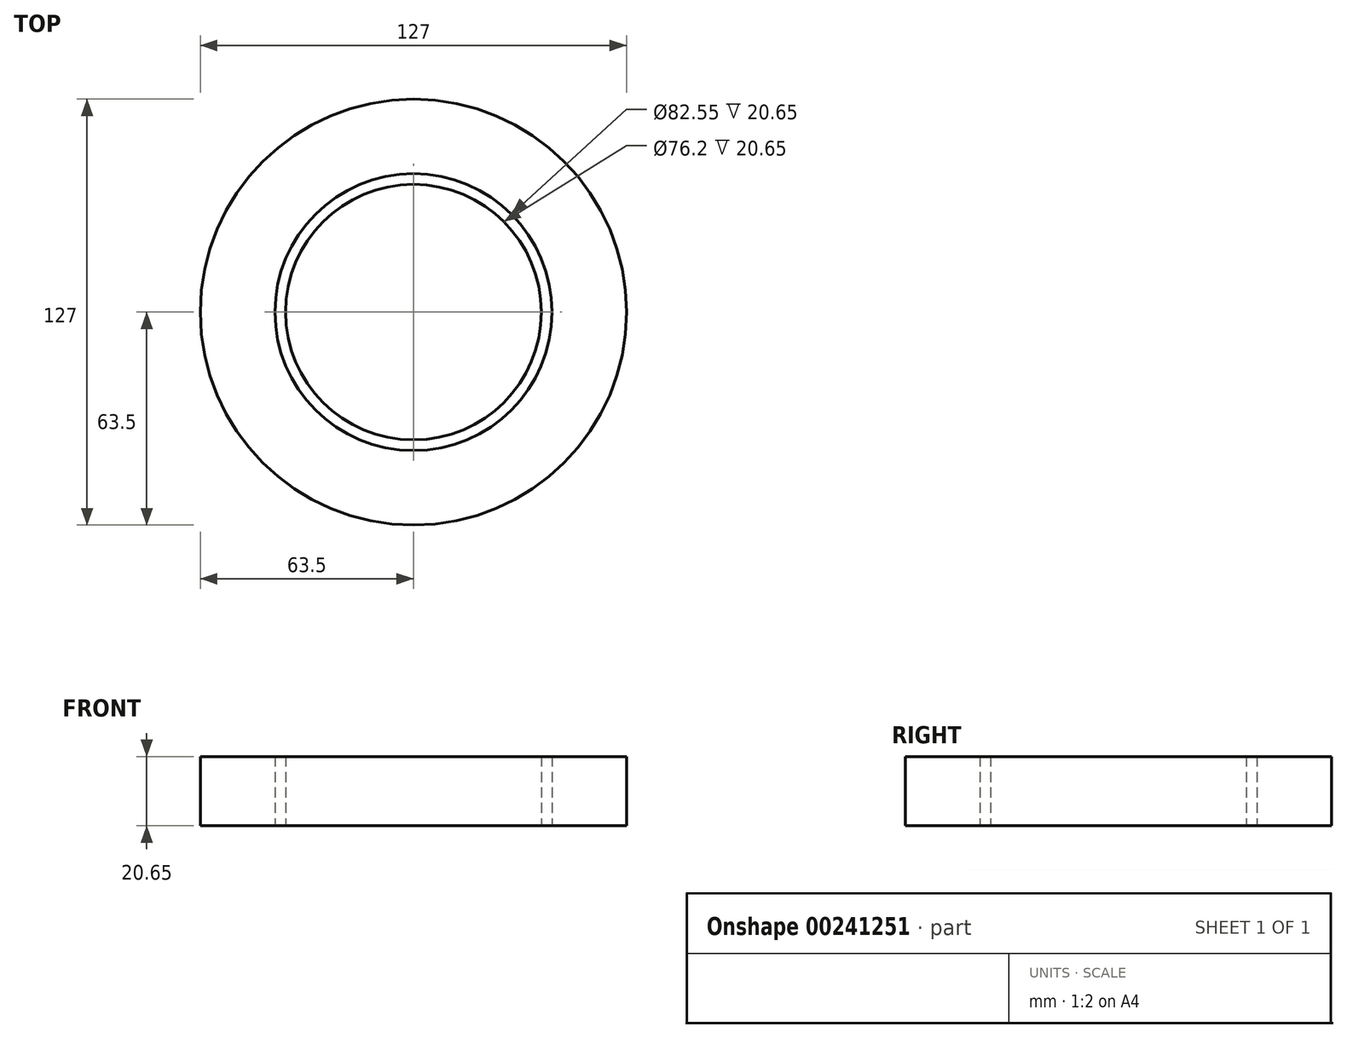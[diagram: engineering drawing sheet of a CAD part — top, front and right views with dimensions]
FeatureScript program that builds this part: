
annotation { "Feature Type Name" : "Feature", "Feature Type Description" : "" }
export const myFeature = defineFeature(function(context is Context, id is Id, definition is map)
    precondition{}
    {
        {
            var Q0;
            Q0=qCreatedBy(makeId("Front.planeOp"),FACE);
            var sketch = newSketch(context, id + "F0", { "sketchPlane" : qUnion([Q0])});
            skLineSegment(sketch, "E0.bottom", {"start": v(0, 0) * mm, "end": v(-3.17, 0) * mm});
            skLineSegment(sketch, "E0.top", {"start": v(0, 20.65) * mm, "end": v(-3.18, 20.65) * mm});
            skLineSegment(sketch, "E0.left", {"start": v(0, 0) * mm, "end": v(0, 20.65) * mm});
            skLineSegment(sketch, "E0.right", {"start": v(-3.17, 0) * mm, "end": v(-3.18, 20.65) * mm});
            skLineSegment(sketch, "E1", {"start": v(38.1, 0) * mm, "end": v(38.1, 23.76) * mm});
            skSolve(sketch);
        }
        {
            var Q0;
            Q0 = qSketchRegion(id + "F0", true);
            var Q1;
            Q1=sQuery(id+"F0.wireOp",EDGE,"E1");
            revolve(context, id + "F1", {"entities" : qUnion([Q0]), "axis" : qUnion([Q1]), "revolveType" : RevolveType.FULL});
        }
        {
            var Q0;
            Q0=qCreatedBy(makeId("Front.planeOp"),FACE);
            var sketch = newSketch(context, id + "F2", { "sketchPlane" : qUnion([Q0])});
            skLineSegment(sketch, "E2", {"start": v(-3.18, 0) * mm, "end": v(-3.18, 20.65) * mm});
            skLineSegment(sketch, "E3.bottom", {"start": v(-3.18, 0) * mm, "end": v(-25.4, 0) * mm});
            skLineSegment(sketch, "E3.top", {"start": v(-3.18, 20.65) * mm, "end": v(-25.4, 20.65) * mm});
            skLineSegment(sketch, "E3.right", {"start": v(-25.4, 0) * mm, "end": v(-25.4, 20.65) * mm});
            skLineSegment(sketch, "E4", {"start": v(38.1, -7.75) * mm, "end": v(38.1, 26.44) * mm});
            skSolve(sketch);
        }
        {
            var Q0;
            Q0 = qSketchRegion(id + "F2", true);
            var Q1;
            Q1=sQuery(id+"F2.wireOp",EDGE,"E4");
            revolve(context, id + "F3", {"entities" : qUnion([Q0]), "axis" : qUnion([Q1]), "revolveType" : RevolveType.FULL});
        }
    });
